# Revit family: STORA-LK-I-D0950-8xx-OSx
name_source: partatom
category: Leuchten
revit_build: Autodesk Revit 2017 (Build: 20190508_0315(x64)
units: mm (PartAtom-declared; Revit-internal decimal feet)

## family parameters
Basisbauteil = Fläche
Beim Laden mit Abzugskörper schneiden = Nein
Bemaßung runder Anschluss = Durchmesser verwenden
Gemeinsam genutzt = Nein
Lichtquelle = Ja
OmniClass-Nummer = 23.80.70.11
OmniClass-Titel = Luminaries for Internal Lighting
Raumberechnungspunkt = Nein
Teiletyp = Normal

## types (4) — shared parameters
Baugruppenkennzeichen = D5020200
Datei für fotometrisches Netz = STORA-LK-I-LED D0950840 OS.IES
Emissionsform beim Rendern sichtbar = Nein
Farbfilter = 16777215
Farbtemperaturverschiebung bei Dämpfen der Lampe = <Keine Auswahl>
Hersteller = RIDI Leuchten GmbH
Lampe = LED
Neigungswinkel = 90.00°
Scheinlast = 114 VA
URL = www.spectral-lighting.com
Von Kreisdurchmesser aussenden = 940 mm  [stored 3.08399 ft]
brand = Spectral
conformity mark = CE
electrical safety class = 1
height = 100 mm  [stored 0.328084 ft]
ingress protection (IP) code = IP20
length = 950 mm  [stored 3.1168 ft]
nominal frequency = 50-60Hz
nominal voltage = 230
rated input power = 114
voltage type (AC, DC, UC) = AC
weight = 14kg
width = 950 mm  [stored 3.1168 ft]
zero-valued in all types: Vorgabe-Ansicht

## per-type parameters (varying)
| type | Modell |
| STORA-LK-I D0950/830 OS | SPC0620050 |
| STORA-LK-I D0950/830 OS-DA | SPC0630050 |
| STORA-LK-I D0950/840 OS | SPC0620051 |
| STORA-LK-I D0950/840 OS-DA | SPC0630051 |

note: column(s) folded — value = type name in every type: product name

note: [stored X ft] marks values corroborated as IEEE doubles in the binary element streams (Revit-internal decimal feet)
